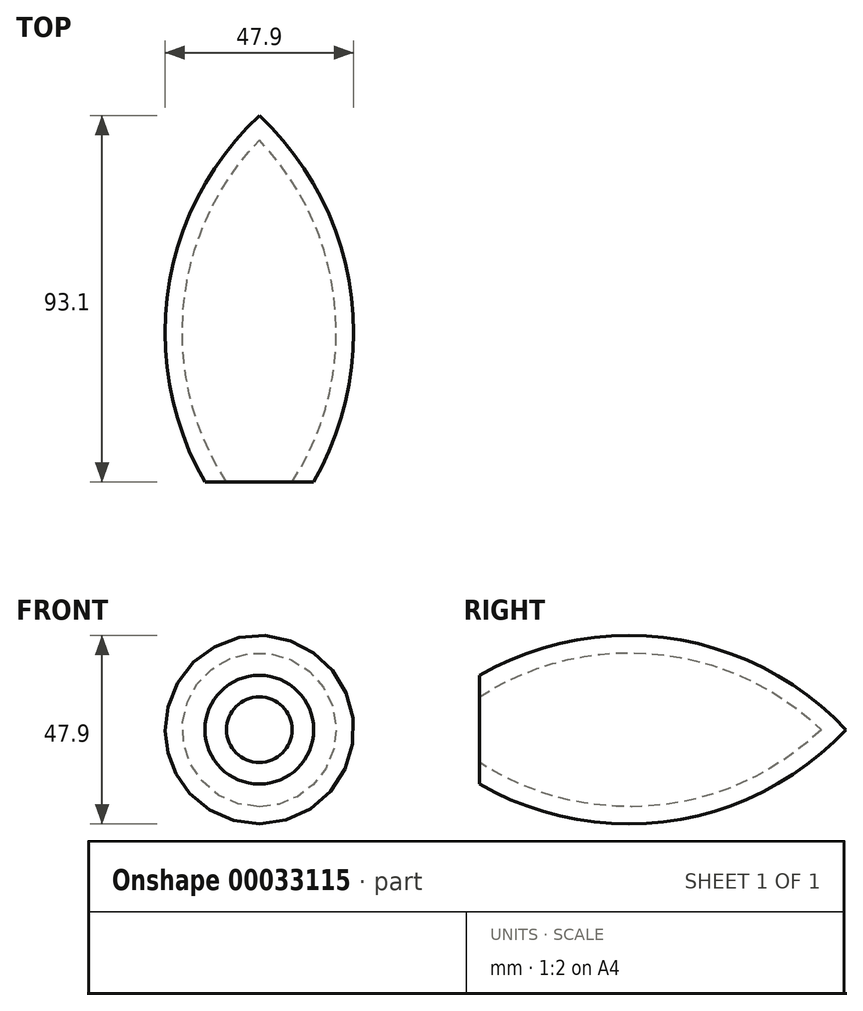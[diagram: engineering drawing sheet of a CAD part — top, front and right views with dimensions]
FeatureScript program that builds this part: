
annotation { "Feature Type Name" : "Feature", "Feature Type Description" : "" }
export const myFeature = defineFeature(function(context is Context, id is Id, definition is map)
    precondition{}
    {
        {
            var Q0;
            Q0=qCreatedBy(makeId("Top.planeOp"),FACE);
            var sketch = newSketch(context, id + "F0", { "sketchPlane" : qUnion([Q0])});
            skLineSegment(sketch, "E0", {"start": v(0, 68.84) * mm, "end": v(0, -62.84) * mm, "construction": true});
            skArc(sketch, "E1", {"start": v(0, 53.72) * mm, "mid": v(-19.23, 11.75) * mm, "end": v(-8.34, -33.12) * mm});
            skArc(sketch, "E2", {"start": v(0, 59.98) * mm, "mid": v(-23.12, 15.84) * mm, "end": v(-13.82, -33.12) * mm});
            skLineSegment(sketch, "E3", {"start": v(0, 59.98) * mm, "end": v(0, 53.72) * mm});
            skLineSegment(sketch, "E4", {"start": v(-13.82, -33.12) * mm, "end": v(-8.34, -33.12) * mm});
            skSolve(sketch);
        }
        {
            var Q0;
            Q0=makeQuery(id+"F0.imprint","IMPRINT",FACE,{"disambiguationData":[TD([[makeQuery(id+"F0.imprint","IMPRINT",EDGE,{"derivedFrom":sQuery(id+"F0.wireOp",EDGE,"E1")}),-1.0]])]});
            var Q1;
            Q1=sQuery(id+"F0.wireOp",EDGE,"E0");
            revolve(context, id + "F1", {"entities" : qUnion([Q0]), "axis" : qUnion([Q1]), "revolveType" : RevolveType.FULL});
        }
    });
